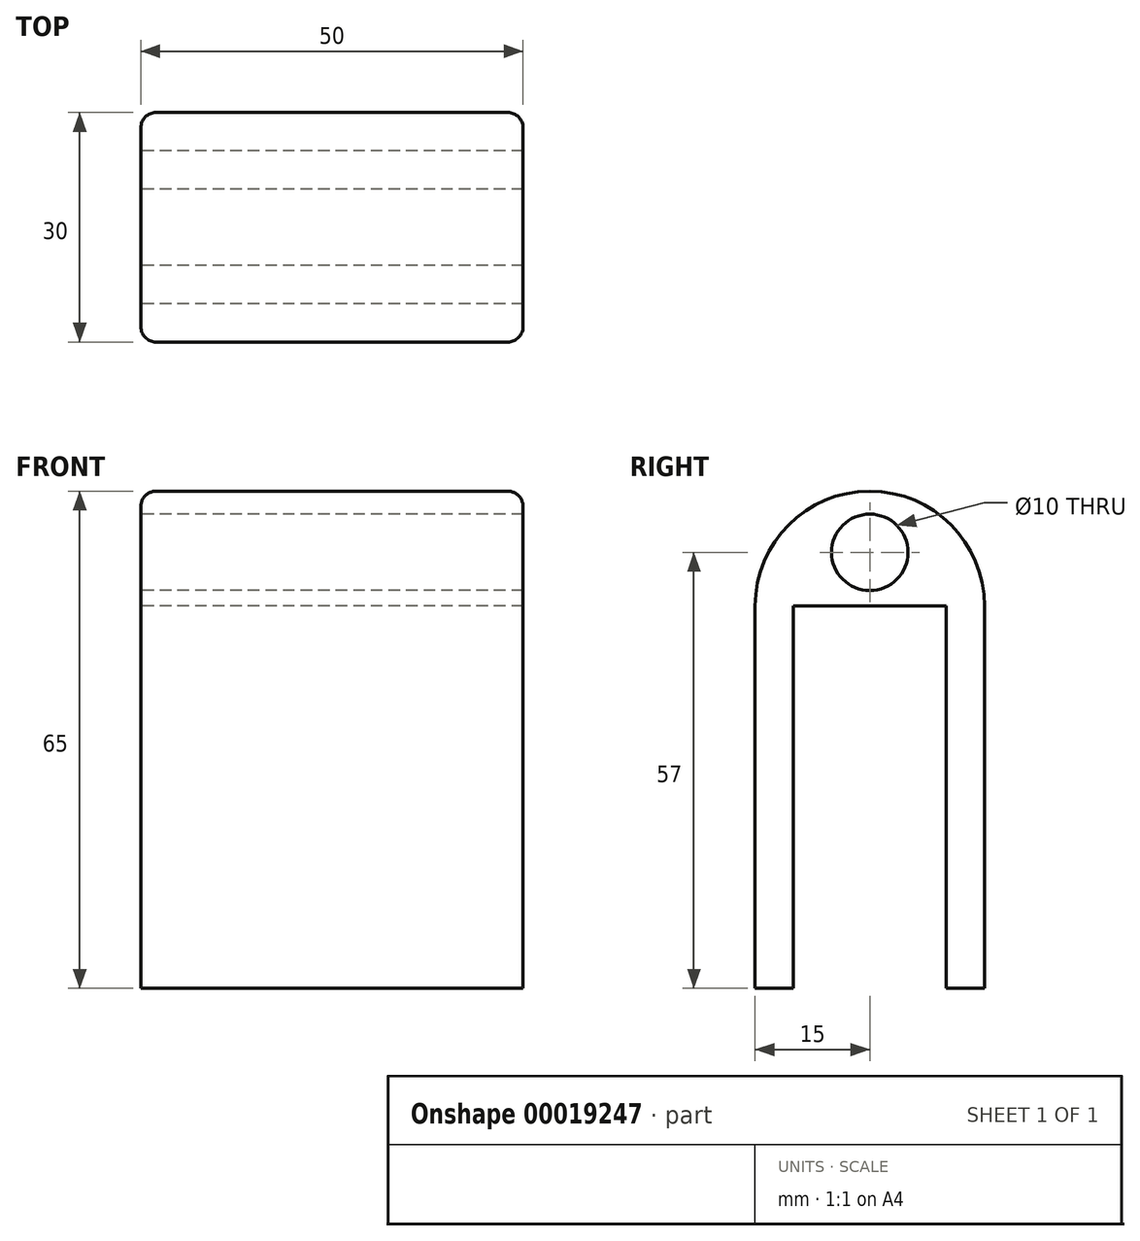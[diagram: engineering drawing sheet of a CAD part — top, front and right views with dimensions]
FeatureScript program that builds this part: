
annotation { "Feature Type Name" : "Feature", "Feature Type Description" : "" }
export const myFeature = defineFeature(function(context is Context, id is Id, definition is map)
    precondition{}
    {
        {
            var Q0;
            Q0=qCreatedBy(makeId("Right.planeOp"),FACE);
            var sketch = newSketch(context, id + "F0", { "sketchPlane" : qUnion([Q0])});
            skLineSegment(sketch, "E0.rect.bottom", {"start": v(-10, 25) * mm, "end": v(10, 25) * mm});
            skLineSegment(sketch, "E0.rect.top", {"start": v(-15, -25) * mm, "end": v(-10, -25) * mm});
            skLineSegment(sketch, "E0.rect.left", {"start": v(-15, 25) * mm, "end": v(-15, -25) * mm});
            skLineSegment(sketch, "E0.rect.right", {"start": v(15, 25) * mm, "end": v(15, -25) * mm});
            skPoint(sketch, "E0.rect.middle", {"position": v(0, 0) * mm});
            skLineSegment(sketch, "E1.rect.top", {"start": v(10, 25) * mm, "end": v(-10, 25) * mm});
            skLineSegment(sketch, "E1.rect.left", {"start": v(10, -25) * mm, "end": v(10, 25) * mm});
            skLineSegment(sketch, "E1.rect.right", {"start": v(-10, -25) * mm, "end": v(-10, 25) * mm});
            skArc(sketch, "E2", {"start": v(15, 25) * mm, "mid": v(0, 40) * mm, "end": v(-15, 25) * mm});
            skLineSegment(sketch, "E3.trimOffspring", {"start": v(10, -25) * mm, "end": v(15, -25) * mm});
            skCircle(sketch, "E4", {"center": v(0, 32) * mm, "radius": 5 * mm});
            skSolve(sketch);
        }
        {
            var Q0;
            Q0 = qSketchRegion(id + "F0", true);
            extrude(context, id + "F1", {"entities" : qUnion([Q0]), "depth" : 50 * mm});
        }
        {
            var Q0;
            Q0=makeQuery(id+"F1.opExtrude","SWEPT_BODY",BODY,{"disambiguationData":[OSD([sQuery(id+"F0.wireOp",EDGE,"E0.rect.top"),sQuery(id+"F0.wireOp",EDGE,"E0.rect.left"),sQuery(id+"F0.wireOp",EDGE,"E0.rect.right"),sQuery(id+"F0.wireOp",EDGE,"E1.rect.top"),sQuery(id+"F0.wireOp",EDGE,"E1.rect.left"),sQuery(id+"F0.wireOp",EDGE,"E1.rect.right"),sQuery(id+"F0.wireOp",EDGE,"E2"),sQuery(id+"F0.wireOp",EDGE,"E3.trimOffspring"),sQuery(id+"F0.wireOp",EDGE,"E4")])]});
            transform(context, id + "F2", {"entities" : qUnion([Q0]), "transformType" : TransformType.TRANSLATION_3D, "dx" : 0 * mm, "dy" : 0 * mm, "dz" : 0 * mm, "makeCopy" : true});
        }
        {
            var Q0;
            Q0=makeQuery(id+"F2.opPattern","COPY",BODY,{"derivedFrom":makeQuery(id+"F1.opExtrude","SWEPT_BODY",BODY,{"disambiguationData":[OSD([sQuery(id+"F0.wireOp",EDGE,"E0.rect.top"),sQuery(id+"F0.wireOp",EDGE,"E0.rect.left"),sQuery(id+"F0.wireOp",EDGE,"E0.rect.right"),sQuery(id+"F0.wireOp",EDGE,"E1.rect.top"),sQuery(id+"F0.wireOp",EDGE,"E1.rect.left"),sQuery(id+"F0.wireOp",EDGE,"E1.rect.right"),sQuery(id+"F0.wireOp",EDGE,"E2"),sQuery(id+"F0.wireOp",EDGE,"E3.trimOffspring"),sQuery(id+"F0.wireOp",EDGE,"E4")])]}),"instanceName":"1"});
            deleteBodies(context, id + "F3", {"entities" : qUnion([Q0])});
        }
        {
            var Q0;
            Q0=makeQuery(id+"F1.opExtrude","SWEPT_BODY",BODY,{"disambiguationData":[OSD([sQuery(id+"F0.wireOp",EDGE,"E0.rect.top"),sQuery(id+"F0.wireOp",EDGE,"E0.rect.left"),sQuery(id+"F0.wireOp",EDGE,"E0.rect.right"),sQuery(id+"F0.wireOp",EDGE,"E1.rect.top"),sQuery(id+"F0.wireOp",EDGE,"E1.rect.left"),sQuery(id+"F0.wireOp",EDGE,"E1.rect.right"),sQuery(id+"F0.wireOp",EDGE,"E2"),sQuery(id+"F0.wireOp",EDGE,"E3.trimOffspring"),sQuery(id+"F0.wireOp",EDGE,"E4")])]});
            transform(context, id + "F4", {"entities" : qUnion([Q0]), "transformType" : TransformType.TRANSLATION_3D, "dx" : 0 * mm, "dy" : 0 * mm, "dz" : 0 * mm, "makeCopy" : true});
        }
        {
            var Q0;
            Q0=makeQuery(id+"F4.opPattern","COPY",EDGE,{"derivedFrom":makeQuery(id+"F1.opExtrude","CAP_EDGE",EDGE,{"disambiguationData":[OSD([sQuery(id+"F0.wireOp",EDGE,"E0.rect.left")])],"isStart":false}),"instanceName":"1"});
            var Q1;
            Q1=makeQuery(id+"F4.opPattern","COPY",EDGE,{"derivedFrom":makeQuery(id+"F1.opExtrude","CAP_EDGE",EDGE,{"disambiguationData":[OSD([sQuery(id+"F0.wireOp",EDGE,"E2")])],"isStart":false}),"instanceName":"1"});
            var Q2;
            Q2=makeQuery(id+"F4.opPattern","COPY",EDGE,{"derivedFrom":makeQuery(id+"F1.opExtrude","CAP_EDGE",EDGE,{"disambiguationData":[OSD([sQuery(id+"F0.wireOp",EDGE,"E0.rect.right")])],"isStart":false}),"instanceName":"1"});
            var Q3;
            Q3=makeQuery(id+"F4.opPattern","COPY",EDGE,{"derivedFrom":makeQuery(id+"F1.opExtrude","CAP_EDGE",EDGE,{"disambiguationData":[OSD([sQuery(id+"F0.wireOp",EDGE,"E0.rect.left")])],"isStart":true}),"instanceName":"1"});
            var Q4;
            Q4=makeQuery(id+"F1.opExtrude","CAP_EDGE",EDGE,{"disambiguationData":[OSD([sQuery(id+"F0.wireOp",EDGE,"E2")])],"isStart":true});
            var Q5;
            Q5=makeQuery(id+"F4.opPattern","COPY",EDGE,{"derivedFrom":makeQuery(id+"F1.opExtrude","CAP_EDGE",EDGE,{"disambiguationData":[OSD([sQuery(id+"F0.wireOp",EDGE,"E0.rect.right")])],"isStart":true}),"instanceName":"1"});
            fillet(context, id + "F5", {"entities" : qUnion([Q0, Q1, Q2, Q3, Q4, Q5]), "radius" : 2 * mm, "tangentPropagation" : true, "allowEdgeOverflow" : false});
        }
        {
            var Q0;
            Q0=makeQuery(id+"F1.opExtrude","SWEPT_BODY",BODY,{"disambiguationData":[OSD([sQuery(id+"F0.wireOp",EDGE,"E0.rect.top"),sQuery(id+"F0.wireOp",EDGE,"E0.rect.left"),sQuery(id+"F0.wireOp",EDGE,"E0.rect.right"),sQuery(id+"F0.wireOp",EDGE,"E1.rect.top"),sQuery(id+"F0.wireOp",EDGE,"E1.rect.left"),sQuery(id+"F0.wireOp",EDGE,"E1.rect.right"),sQuery(id+"F0.wireOp",EDGE,"E2"),sQuery(id+"F0.wireOp",EDGE,"E3.trimOffspring"),sQuery(id+"F0.wireOp",EDGE,"E4")])]});
            deleteBodies(context, id + "F6", {"entities" : qUnion([Q0])});
        }
    });
